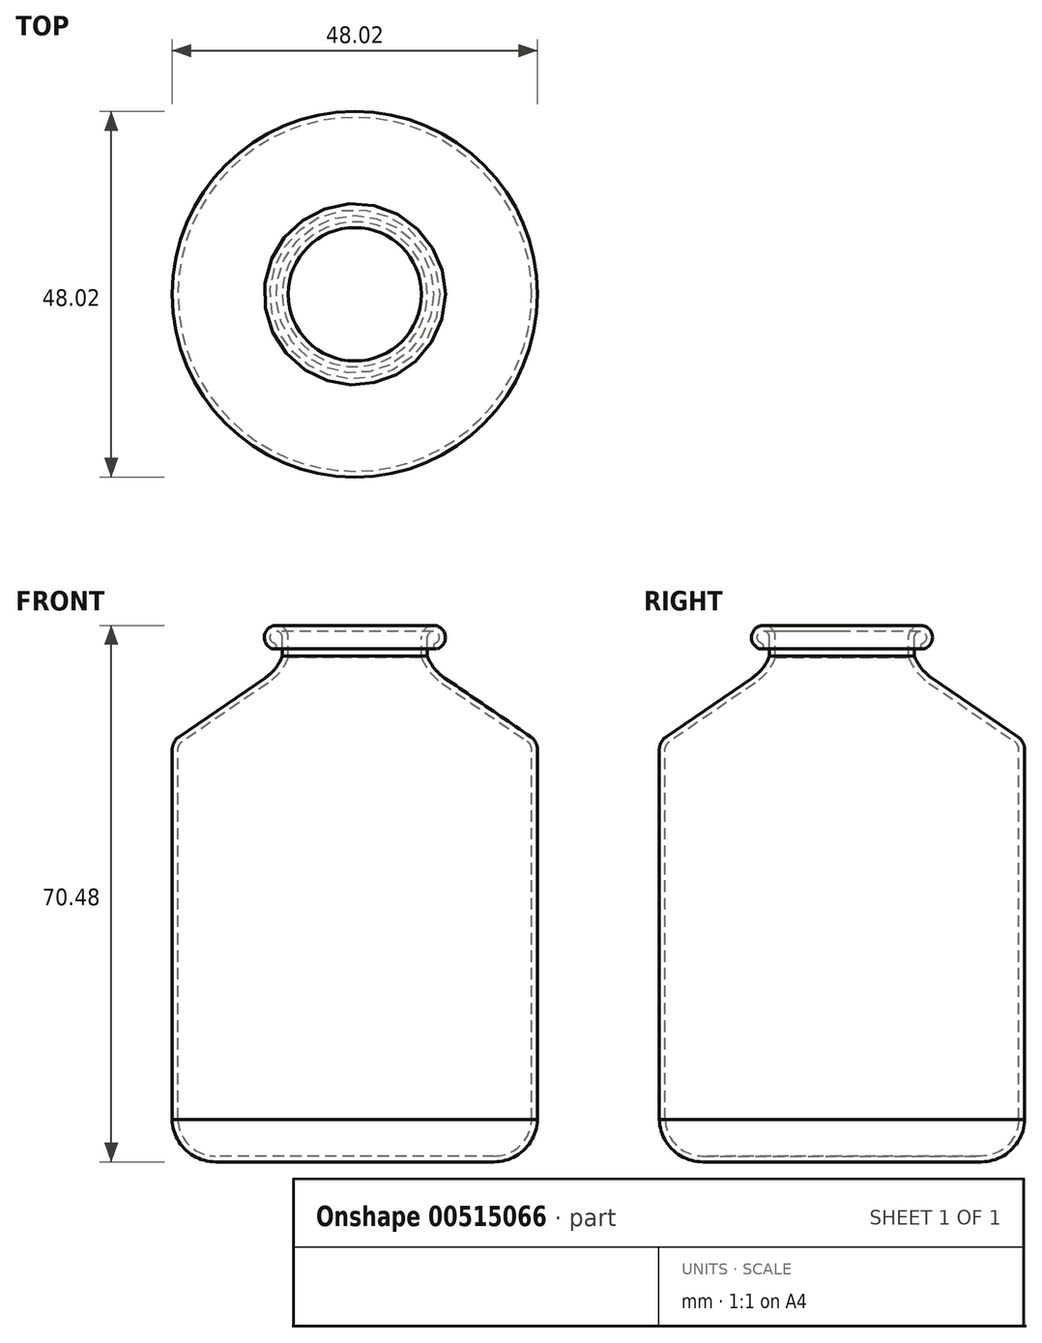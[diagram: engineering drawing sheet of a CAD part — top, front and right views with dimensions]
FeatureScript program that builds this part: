
annotation { "Feature Type Name" : "Feature", "Feature Type Description" : "" }
export const myFeature = defineFeature(function(context is Context, id is Id, definition is map)
    precondition{}
    {
        {
            var Q0;
            Q0=qCreatedBy(makeId("Front.planeOp"),FACE);
            var sketch = newSketch(context, id + "F0", { "sketchPlane" : qUnion([Q0])});
            skLineSegment(sketch, "E0", {"start": v(0, 0) * mm, "end": v(-18.3, 0) * mm});
            skArc(sketch, "E1", {"start": v(-18.3, 0) * mm, "mid": v(-22.28, 1.62) * mm, "end": v(-24, 5.57) * mm});
            skLineSegment(sketch, "E2", {"start": v(-24, 5.57) * mm, "end": v(-24, 54.13) * mm});
            skArc(sketch, "E3", {"start": v(-24, 54.13) * mm, "mid": v(-23.76, 55.11) * mm, "end": v(-23.1, 55.87) * mm});
            skLineSegment(sketch, "E4", {"start": v(-23.1, 55.87) * mm, "end": v(-11.82, 63.56) * mm});
            skArc(sketch, "E5", {"start": v(-11.82, 63.56) * mm, "mid": v(-10.46, 64.83) * mm, "end": v(-9.52, 66.44) * mm});
            skLineSegment(sketch, "E6", {"start": v(-9.52, 66.44) * mm, "end": v(-9.52, 68.9) * mm});
            skArc(sketch, "E7", {"start": v(-9.52, 68.9) * mm, "mid": v(-10.8, 69.57) * mm, "end": v(-10.6, 68.15) * mm});
            skArc(sketch, "E8.0", {"start": v(-8.75, 68.9) * mm, "mid": v(-11.23, 70.2) * mm, "end": v(-10.86, 67.43) * mm});
            skLineSegment(sketch, "E8.1", {"start": v(-8.75, 66.3) * mm, "end": v(-8.75, 68.9) * mm});
            skArc(sketch, "E8.2", {"start": v(-11.4, 62.93) * mm, "mid": v(-9.82, 64.41) * mm, "end": v(-8.75, 66.3) * mm});
            skLineSegment(sketch, "E8.3", {"start": v(-22.66, 55.24) * mm, "end": v(-11.4, 62.93) * mm});
            skLineSegment(sketch, "E8.4", {"start": v(0, 0.76) * mm, "end": v(-18.3, 0.76) * mm});
            skArc(sketch, "E8.5", {"start": v(-18.3, 0.76) * mm, "mid": v(-21.75, 2.16) * mm, "end": v(-23.24, 5.58) * mm});
            skLineSegment(sketch, "E8.6", {"start": v(-23.24, 5.58) * mm, "end": v(-23.24, 54.13) * mm});
            skArc(sketch, "E8.7", {"start": v(-23.24, 54.13) * mm, "mid": v(-23.09, 54.76) * mm, "end": v(-22.66, 55.24) * mm});
            skArc(sketch, "E9", {"start": v(-10.6, 68.15) * mm, "mid": v(-10.37, 67.66) * mm, "end": v(-10.86, 67.43) * mm});
            skLineSegment(sketch, "E10", {"start": v(0, 0.76) * mm, "end": v(0, 0) * mm});
            skSolve(sketch);
        }
        {
            var Q0;
            Q0=makeQuery(id+"F0.imprint","IMPRINT",FACE,{"disambiguationData":[TD([[makeQuery(id+"F0.imprint","IMPRINT",EDGE,{"derivedFrom":sQuery(id+"F0.wireOp",EDGE,"E0")}),-1.0]])]});
            var Q1;
            Q1=sQuery(id+"F0.wireOp",EDGE,"E10");
            revolve(context, id + "F1", {"entities" : qUnion([Q0]), "axis" : qUnion([Q1]), "revolveType" : RevolveType.FULL});
        }
    });
